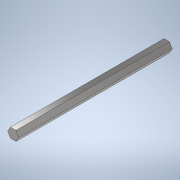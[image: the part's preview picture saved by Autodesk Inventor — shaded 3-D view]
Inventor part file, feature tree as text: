
AUTODESK INVENTOR PART (.ipt)
format: ipt  version: 2020 (Build 240168000, 168)  size: 101,376 bytes
history: native  units: in
note: dims shown in document units (in); Inventor stores cm internally (conversion verified against a paired STEP export)
features: extrude x1, sketch x1
ambient origin geometry x8: Origin, YZ Plane, XZ Plane, XY Plane, X Axis, Y Axis, Z Axis, Center Point
bodies: Solid1 (feature_tree)
feature tree (2):
  extrude  "Extrusion1"  Depth=8.0in TaperAngle=0.0deg
  sketch  "Sketch1"  dims[d0=0.5in d1=8.0in d2=0.0in]
